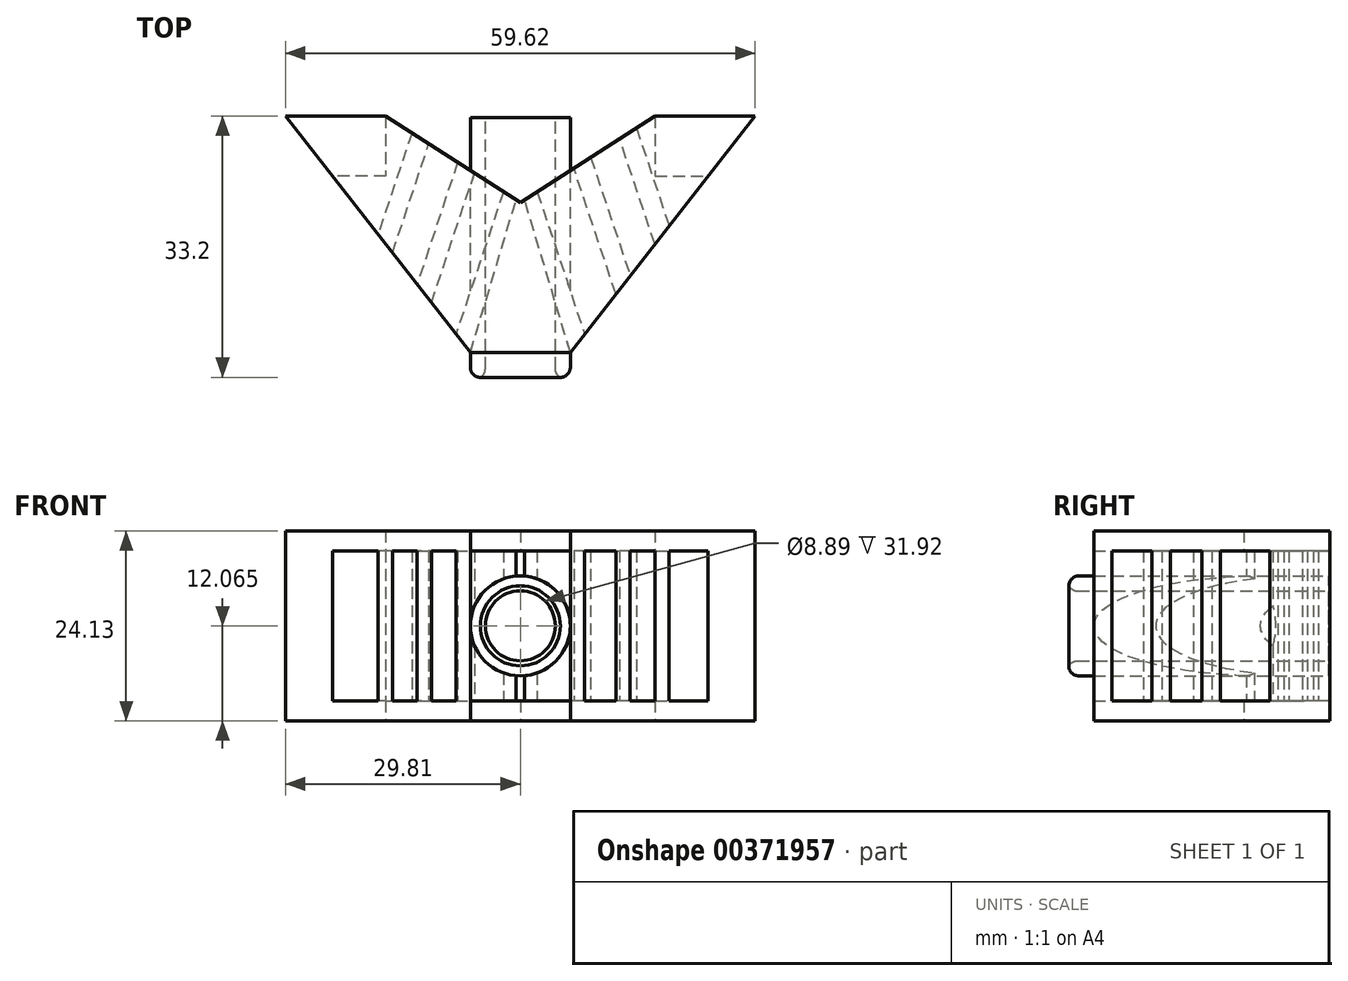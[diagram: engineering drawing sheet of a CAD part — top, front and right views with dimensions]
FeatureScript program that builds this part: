
annotation { "Feature Type Name" : "Feature", "Feature Type Description" : "" }
export const myFeature = defineFeature(function(context is Context, id is Id, definition is map)
    precondition{}
    {
        {
            var Q0;
            Q0=qCreatedBy(makeId("Top.planeOp"),FACE);
            var sketch = newSketch(context, id + "F0", { "sketchPlane" : qUnion([Q0])});
            skLineSegment(sketch, "E0.top", {"start": v(6.35, -9.53) * mm, "end": v(-6.35, -9.53) * mm});
            skPoint(sketch, "E0.middle", {"position": v(0, 0) * mm});
            skLineSegment(sketch, "E1", {"start": v(6.35, -9.53) * mm, "end": v(29.8, 20.5) * mm});
            skLineSegment(sketch, "E2", {"start": v(29.8, 20.5) * mm, "end": v(17.1, 20.5) * mm});
            skLineSegment(sketch, "E3", {"start": v(17.1, 20.5) * mm, "end": v(0, 9.53) * mm});
            skLineSegment(sketch, "E4", {"start": v(-6.35, -9.53) * mm, "end": v(-29.8, 20.5) * mm});
            skLineSegment(sketch, "E5", {"start": v(-29.8, 20.5) * mm, "end": v(-17.1, 20.5) * mm});
            skLineSegment(sketch, "E6", {"start": v(-17.1, 20.5) * mm, "end": v(0, 9.53) * mm});
            skSolve(sketch);
        }
        {
            var Q0;
            Q0 = qSketchRegion(id + "F0", true);
            extrude(context, id + "F1", {"entities" : qUnion([Q0]), "depth" : 24.13 * mm, "offsetDistance" : 25.4 * mm});
        }
        {
            var Q0;
            Q0=makeQuery(id+"F1.opExtrude","SWEPT_FACE",FACE,{"disambiguationData":[OSD([sQuery(id+"F0.wireOp",EDGE,"E0.top")])]});
            var sketch = newSketch(context, id + "F2", { "sketchPlane" : qUnion([Q0])});
            skPoint(sketch, "E7", {"position": v(-6.35, 24.13) * mm});
            skPoint(sketch, "E8", {"position": v(6.35, 24.13) * mm});
            skPoint(sketch, "E9", {"position": v(-6.35, 0) * mm});
            skPoint(sketch, "E10", {"position": v(6.35, 0) * mm});
            skPoint(sketch, "E11", {"position": v(-6.35, 2.54) * mm});
            skPoint(sketch, "E12", {"position": v(6.35, 2.54) * mm});
            skPoint(sketch, "E13", {"position": v(-6.35, 21.6) * mm});
            skPoint(sketch, "E14", {"position": v(6.35, 21.6) * mm});
            skLineSegment(sketch, "E15", {"start": v(-67.78, 21.6) * mm, "end": v(69.68, 21.6) * mm});
            skLineSegment(sketch, "E16", {"start": v(69.68, 21.6) * mm, "end": v(69.68, 2.54) * mm});
            skLineSegment(sketch, "E17", {"start": v(69.68, 2.54) * mm, "end": v(-66.45, 2.54) * mm});
            skLineSegment(sketch, "E18", {"start": v(-66.45, 2.54) * mm, "end": v(-67.78, 21.6) * mm});
            skSolve(sketch);
        }
        {
            var Q0;
            Q0 = qSketchRegion(id + "F2", true);
            extrude(context, id + "F3", {"entities" : qUnion([Q0]), "operationType" : NewBodyOperationType.REMOVE, "oppositeDirection" : true, "depth" : 53.34 * mm, "offsetDistance" : 25.4 * mm});
        }
        {
            var Q0;
            Q0=makeQuery(id+"F3.boolean.opBoolean","COPY",FACE,{"derivedFrom":makeQuery(id+"F3.opExtrude","SWEPT_FACE",FACE,{"disambiguationData":[OSD([sQuery(id+"F2.wireOp",EDGE,"E17")])]})});
            var sketch = newSketch(context, id + "F4", { "sketchPlane" : qUnion([Q0])});
            skLineSegment(sketch, "E19", {"start": v(-0.53, 9.87) * mm, "end": v(-2.14, 10.9) * mm});
            skLineSegment(sketch, "E20", {"start": v(-2.14, 10.9) * mm, "end": v(-8.17, -7.2) * mm});
            skLineSegment(sketch, "E21", {"start": v(-8.17, -7.2) * mm, "end": v(-6.35, -9.53) * mm});
            skPoint(sketch, "E22", {"position": v(-11.3, -3.2) * mm});
            skLineSegment(sketch, "E23", {"start": v(-11.3, -3.2) * mm, "end": v(-5.81, 13.25) * mm});
            skLineSegment(sketch, "E24", {"start": v(-5.81, 13.25) * mm, "end": v(-7.95, 14.63) * mm});
            skLineSegment(sketch, "E25", {"start": v(-7.95, 14.63) * mm, "end": v(-13.12, -0.87) * mm});
            skLineSegment(sketch, "E26", {"start": v(-13.12, -0.87) * mm, "end": v(-11.3, -3.2) * mm});
            skLineSegment(sketch, "E27", {"start": v(-17.1, 20.5) * mm, "end": v(-17.1, 12.88) * mm});
            skLineSegment(sketch, "E28", {"start": v(-17.1, 12.88) * mm, "end": v(-23.85, 12.88) * mm});
            skLineSegment(sketch, "E29", {"start": v(-23.85, 12.88) * mm, "end": v(-29.8, 20.5) * mm});
            skLineSegment(sketch, "E30", {"start": v(-29.8, 20.5) * mm, "end": v(-17.1, 20.5) * mm});
            skLineSegment(sketch, "E31", {"start": v(17.1, 20.5) * mm, "end": v(17.1, 12.88) * mm});
            skLineSegment(sketch, "E32", {"start": v(17.1, 12.88) * mm, "end": v(23.85, 12.88) * mm});
            skLineSegment(sketch, "E33", {"start": v(23.85, 12.88) * mm, "end": v(29.8, 20.5) * mm});
            skLineSegment(sketch, "E34", {"start": v(29.8, 20.5) * mm, "end": v(17.1, 20.5) * mm});
            skPoint(sketch, "E35", {"position": v(-16.24, 3.14) * mm});
            skLineSegment(sketch, "E36", {"start": v(-16.24, 3.14) * mm, "end": v(-11.63, 16.98) * mm});
            skLineSegment(sketch, "E37", {"start": v(-11.63, 16.98) * mm, "end": v(-13.77, 18.36) * mm});
            skLineSegment(sketch, "E38", {"start": v(-13.77, 18.36) * mm, "end": v(-18.06, 5.47) * mm});
            skLineSegment(sketch, "E39", {"start": v(-18.06, 5.47) * mm, "end": v(-16.24, 3.14) * mm});
            skLineSegment(sketch, "E40", {"start": v(2.14, 10.9) * mm, "end": v(8.17, -7.2) * mm});
            skLineSegment(sketch, "E41", {"start": v(8.17, -7.2) * mm, "end": v(6.35, -9.53) * mm});
            skPoint(sketch, "E42", {"position": v(12.14, -2.12) * mm});
            skLineSegment(sketch, "E43", {"start": v(12.14, -2.12) * mm, "end": v(6.8, 13.89) * mm});
            skLineSegment(sketch, "E44", {"start": v(6.8, 13.89) * mm, "end": v(8.94, 15.26) * mm});
            skLineSegment(sketch, "E45", {"start": v(8.94, 15.26) * mm, "end": v(13.96, 0.21) * mm});
            skLineSegment(sketch, "E46", {"start": v(13.96, 0.21) * mm, "end": v(12.14, -2.12) * mm});
            skLineSegment(sketch, "E47", {"start": v(12.14, -2.12) * mm, "end": v(13.96, 0.21) * mm});
            skPoint(sketch, "E48", {"position": v(17.08, 4.21) * mm});
            skLineSegment(sketch, "E49", {"start": v(17.08, 4.21) * mm, "end": v(12.62, 17.62) * mm});
            skLineSegment(sketch, "E50", {"start": v(12.62, 17.62) * mm, "end": v(14.75, 18.99) * mm});
            skLineSegment(sketch, "E51", {"start": v(14.75, 18.99) * mm, "end": v(18.9, 6.54) * mm});
            skLineSegment(sketch, "E52", {"start": v(18.9, 6.54) * mm, "end": v(17.08, 4.21) * mm});
            skLineSegment(sketch, "E53", {"start": v(-6.35, -9.53) * mm, "end": v(-0.53, 9.87) * mm});
            skLineSegment(sketch, "E54", {"start": v(6.35, -9.52) * mm, "end": v(0.53, 9.87) * mm});
            skLineSegment(sketch, "E55", {"start": v(0.53, 9.87) * mm, "end": v(2.14, 10.9) * mm});
            skSolve(sketch);
        }
        {
            var Q0;
            Q0 = qSketchRegion(id + "F4", true);
            extrude(context, id + "F5", {"entities" : qUnion([Q0]), "operationType" : NewBodyOperationType.ADD, "depth" : 19.05 * mm, "offsetDistance" : 25.4 * mm});
        }
        {
            var Q0;
            Q0=qCreatedBy(makeId("Front.planeOp"),FACE);
            var sketch = newSketch(context, id + "F6", { "sketchPlane" : qUnion([Q0])});
            skCircle(sketch, "E56", {"center": v(0, 12.07) * mm, "radius": 6.35 * mm});
            skCircle(sketch, "E57", {"center": v(0, 12.07) * mm, "radius": 4.45 * mm});
            skSolve(sketch);
        }
        {
            var Q0;
            Q0 = qSketchRegion(id + "F6", true);
            extrude(context, id + "F7", {"entities" : qUnion([Q0]), "operationType" : NewBodyOperationType.ADD, "depth" : 12.7 * mm, "offsetDistance" : 25.4 * mm});
        }
        {
            var Q0;
            Q0=makeQuery(id+"F6.imprint","IMPRINT",FACE,{"disambiguationData":[TD([[makeQuery(id+"F6.imprint","IMPRINT",EDGE,{"derivedFrom":sQuery(id+"F6.wireOp",EDGE,"E56")}),1.0]])]});
            extrude(context, id + "F8", {"entities" : qUnion([Q0]), "operationType" : NewBodyOperationType.ADD, "oppositeDirection" : true, "depth" : 20.32 * mm, "offsetDistance" : 25.4 * mm});
        }
        {
            var Q0;
            Q0=makeQuery(id+"F6.imprint","IMPRINT",FACE,{"disambiguationData":[TD([[makeQuery(id+"F6.imprint","IMPRINT",EDGE,{"derivedFrom":sQuery(id+"F6.wireOp",EDGE,"E57")}),1.0]])]});
            extrude(context, id + "F9", {"entities" : qUnion([Q0]), "operationType" : NewBodyOperationType.REMOVE, "oppositeDirection" : true, "depth" : 50.57 * mm, "offsetDistance" : 25.4 * mm});
        }
        {
            var Q0;
            {var subQ0=sQuery(id+"F6.wireOp",EDGE,"E57");Q0=makeQuery(id+"F9.boolean.opBoolean","COPY",FACE,{"disambiguationData":[TD([makeQuery(id+"F5.opExtrude","SWEPT_FACE",FACE,{"disambiguationData":[OSD([sQuery(id+"F4.wireOp",EDGE,"E54")])]})])],"derivedFrom":makeQuery(id+"F9.opExtrude","CAP_FACE",FACE,{"disambiguationData":[OSD([subQ0])],"isStart":true})});}
            extrude(context, id + "F10", {"entities" : qUnion([Q0]), "operationType" : NewBodyOperationType.REMOVE, "oppositeDirection" : true, "depth" : 25.4 * mm, "offsetDistance" : 25.4 * mm});
        }
        {
            var Q0;
            {var subQ0=sQuery(id+"F6.wireOp",EDGE,"E57");Q0=makeQuery(id+"F9.boolean.opBoolean","COPY",FACE,{"disambiguationData":[TD([makeQuery(id+"F5.opExtrude","SWEPT_FACE",FACE,{"disambiguationData":[OSD([sQuery(id+"F4.wireOp",EDGE,"E53")])]})])],"derivedFrom":makeQuery(id+"F9.opExtrude","CAP_FACE",FACE,{"disambiguationData":[OSD([subQ0])],"isStart":true})});}
            extrude(context, id + "F11", {"entities" : qUnion([Q0]), "operationType" : NewBodyOperationType.REMOVE, "oppositeDirection" : true, "depth" : 25.4 * mm, "offsetDistance" : 25.4 * mm});
        }
        {
            var Q0;
            Q0=makeQuery(id+"F7.opExtrude","CAP_EDGE",EDGE,{"disambiguationData":[OSD([sQuery(id+"F6.wireOp",EDGE,"E56")])],"isStart":false});
            fillet(context, id + "F12", {"entities" : qUnion([Q0]), "radius" : 1.27 * mm, "tangentPropagation" : true, "allowEdgeOverflow" : false});
        }
        {
            var Q0;
            Q0=makeQuery(id+"F7.opExtrude","CAP_EDGE",EDGE,{"disambiguationData":[OSD([sQuery(id+"F6.wireOp",EDGE,"E57")])],"isStart":false});
            fillet(context, id + "F13", {"entities" : qUnion([Q0]), "radius" : 1.27 * mm, "tangentPropagation" : true, "allowEdgeOverflow" : false});
        }
    });
